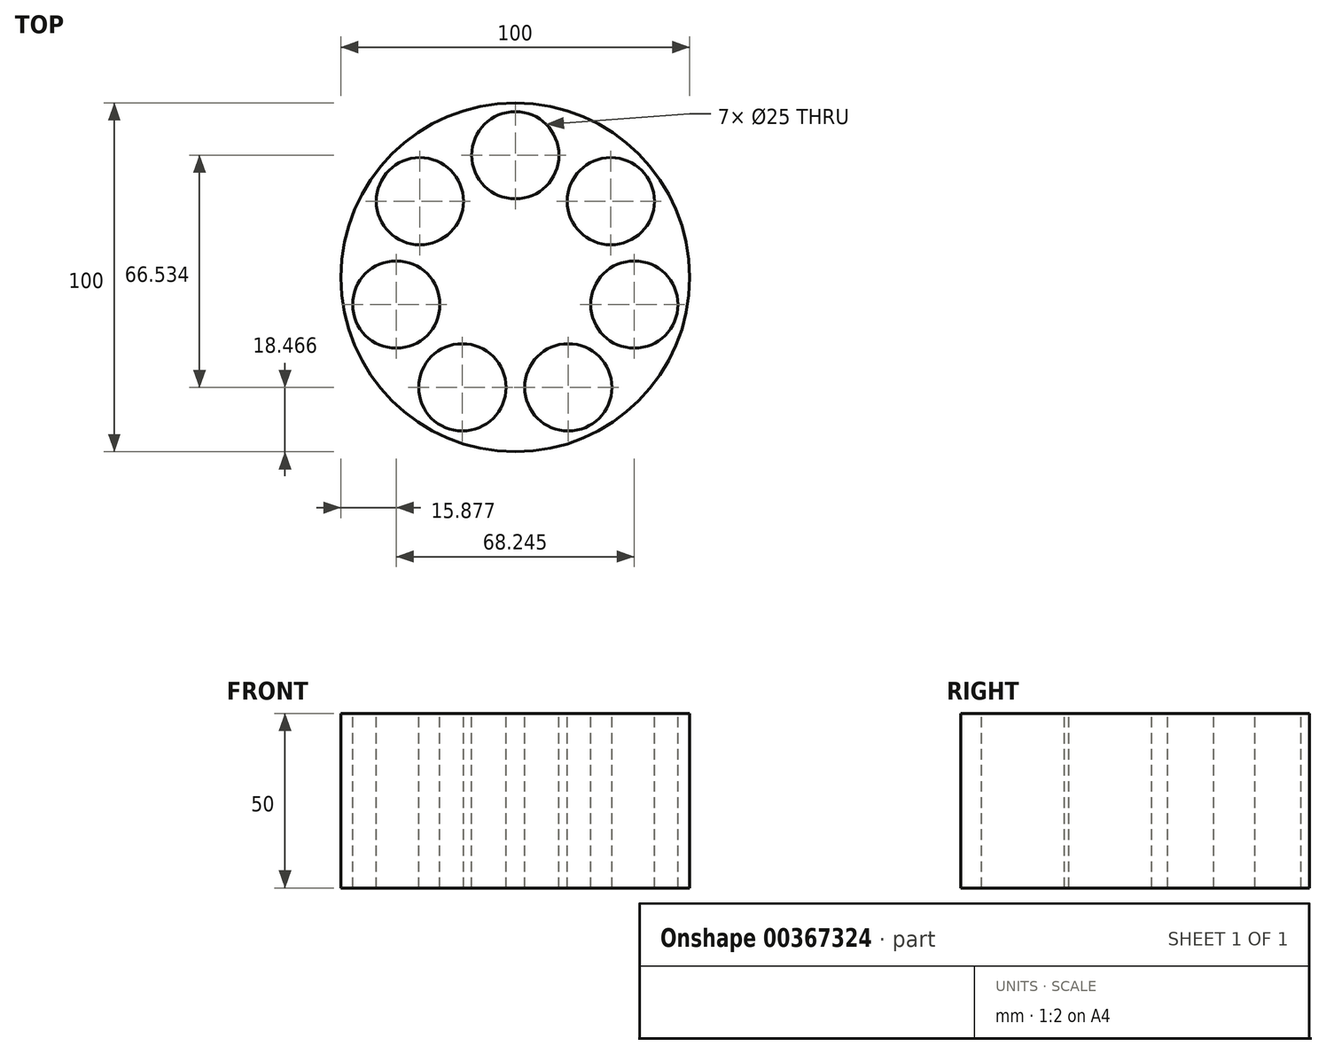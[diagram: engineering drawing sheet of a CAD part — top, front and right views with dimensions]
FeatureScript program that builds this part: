
annotation { "Feature Type Name" : "Feature", "Feature Type Description" : "" }
export const myFeature = defineFeature(function(context is Context, id is Id, definition is map)
    precondition{}
    {
        {
            var Q0;
            Q0=qCreatedBy(makeId("Top.planeOp"),FACE);
            var sketch = newSketch(context, id + "F0", { "sketchPlane" : qUnion([Q0])});
            skCircle(sketch, "E0", {"center": v(0, 0) * mm, "radius": 50 * mm});
            skSolve(sketch);
        }
        {
            var Q0;
            Q0=makeQuery(id+"F0.imprint","IMPRINT",FACE,{"disambiguationData":[TD([[makeQuery(id+"F0.imprint","IMPRINT",EDGE,{"derivedFrom":sQuery(id+"F0.wireOp",EDGE,"E0")}),1.0]])]});
            extrude(context, id + "F1", {"entities" : qUnion([Q0]), "depth" : 50 * mm});
        }
        {
            var Q0;
            Q0=makeQuery(id+"F1.opExtrude","CAP_FACE",FACE,{"disambiguationData":[OSD([sQuery(id+"F0.wireOp",EDGE,"E0")])],"isStart":false});
            var sketch = newSketch(context, id + "F2", { "sketchPlane" : qUnion([Q0])});
            skCircle(sketch, "E1", {"center": v(-15.19, -31.53) * mm, "radius": 12.5 * mm});
            skCircle(sketch, "E2.1.0", {"center": v(15.19, -31.53) * mm, "radius": 12.5 * mm});
            skCircle(sketch, "E2.2.0", {"center": v(34.12, -7.79) * mm, "radius": 12.5 * mm});
            skCircle(sketch, "E2.3.0", {"center": v(27.36, 21.82) * mm, "radius": 12.5 * mm});
            skCircle(sketch, "E2.4.0", {"center": v(0, 35) * mm, "radius": 12.5 * mm});
            skPoint(sketch, "E2.center", {"position": v(0, 0) * mm});
            skCircle(sketch, "E3.1.5.0", {"center": v(-27.36, 21.82) * mm, "radius": 12.5 * mm});
            skCircle(sketch, "E3.1.6.0", {"center": v(-34.12, -7.79) * mm, "radius": 12.5 * mm});
            skSolve(sketch);
        }
        {
            var Q0;
            Q0 = qSketchRegion(id + "F2", true);
            extrude(context, id + "F3", {"entities" : qUnion([Q0]), "operationType" : NewBodyOperationType.REMOVE, "endBound" : BoundingType.UP_TO_NEXT, "oppositeDirection" : true, "depth" : 25 * mm});
        }
    });
